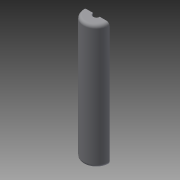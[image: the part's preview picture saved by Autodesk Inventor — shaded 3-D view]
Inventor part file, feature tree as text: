
AUTODESK INVENTOR PART (.ipt)
format: ipt  version: 2014 (Build 180170000, 170)  size: 85,504 bytes
history: native  units: mm
features: extrude x2, sketch x2, fillet x1
ambient origin geometry x8: Origin, YZ Plane, XZ Plane, XY Plane, X Axis, Y Axis, Z Axis, Center Point
bodies: Solid1 (feature_tree)
feature tree (5):
  extrude  "Extrusion1"  Depth=120.65mm
  fillet  "Fillet1"  Radius=120.65mm
  extrude  "Extrusion2"  TaperAngle=0.0deg  [1 undecoded]
  sketch  "Sketch1"  dims[d0=25.4mm d1=6.604mm d2=120.65mm d3=0.0mm]
  sketch  "Sketch3"  dims[d4=3.0mm d5=0.0mm d6=0.0mm]
note: 1 required parameter value undecoded (feature->parameter linkage not recoverable at this tier; creation-order binding heuristic only, values carry confidence <= 0.55)
